# Revit family: PC-1860AB-EB
name_source: partatom
category: Communication Devices
units: mm (PartAtom-declared; Revit-internal decimal feet)

## family parameters
Cut with Voids When Loaded = Yes
Host = Face
Maintain Annotation Orientation = No
OmniClass Number = 23.85.10.11.14
OmniClass Title = Audio Equipment
Part Type = Normal
Room Calculation Point = No
Round Connector Dimension = Use Diameter
Shared = No

## types (1)
- PC-1860AB-EB
    Accessory = Rubber grommet x 2, Paper pattern x 1
    Applicable Cable = Outer diameter : Ø6.5 - Ø12.5 mm.
 Conductor : Solid wire or 7-core wire
 No bridge connection : 0.8 - 10 mm  (AWG18 - AWG7) for solid wire
                      0.8 - 8 mm  (AWG18 - AWG8) for 7-core wire
 Bridge connection : 0.8 - 2.5 mm  (AWG18 - AWG13) for solid wire
                      0.8 - 1.5 mm  (AWG18 - AWG15) for 7-core wire
    Connection = 2x 3-pins Screw terminal (steatite)
    Coverage Angle = Horizontal: 180° (500 Hz), 165° (1 kHz), 115° (2 kHz), 40° (4 kHz) 
Vertical  : 180° (500 Hz), 170° (1 kHz), 160° (2 kHz), 130° (4 kHz)
    Default Elevation = 0 mm  [stored 0 ft]
    Dimension = ∅180 x 8 (exposed section) + 110 (D) mm (∅7.09"  0.31" + 4.33")
    Dimension for Fixing Hole = ∅156±3 mm (6.14"±0.12")
Max. ceiling thickness: 30 mm (1.18")
    Environmental Type = A (indoor application, IP21C)
    Finish = Frame: Steel plate, white (RAL 9016 equivalent), paint
Grille: Steel net, white (RAL 9016 equivalent), paint
Fire dome: Steel plate, black, paint
    Frequency Response = 150 Hz - 20 kHz (peak -20 dB)
    Impedance Tap = 1700
    Impedance Tap Assistance = Type 1700, 3300, 6700, 13000
    Manufacturer = TOA
    Material = OFF-WHITE
    Mesh = Mesh
    Model = PC-1860AB-EB
    Operating Temperature = -10 °C to +55 °C (14 °F to 131 °F)
    Rated Impedance = 100 V line: 1.7 kΩ (6 W), 3.3 kΩ (3 W), 6.7 kΩ (1.5 W)
    Rated Input = 2x 6 W (100 V line)
    SP Line Assistance = Type 70 or 100
    SP Line Voltage = 100
    Sensitivity (SPL) Max. SPL = 92 dB (2x 0.5 W, 1 m) (500 Hz - 5 kHz, pink noise)
102 dB (2x 6 W, 1 m) (500 Hz - 5 kHz, pink noise)
    Sensitivity EN54-24 Max. Sensitivity EN54-24 = 76 dB (2X 0.5 W, 4 m) (100 Hz - 10 kHz, pink noise)
86.9 dB (2X 6 W, 4 m) (100 Hz - 10 kHz, pink noise)
    Speaker Component = 2x 8 cm (3") cone-type
    Speaker Mounting Method = Spring catch
    Steel - Black = Steel - Black finish
    Update info = https://www.sound-toa.com
    Ver = 1.0
    Weight = 1.87 kg (4.13 lb)
    Weight [Kg] (for Schedules/Quantities) = 1.87

note: [stored X ft] marks values corroborated as IEEE doubles in the binary element streams (Revit-internal decimal feet)

## geometry (parser evidence)
native form markers: Blend x2, Sweep x8
no freeform markers — native parametric forms only
